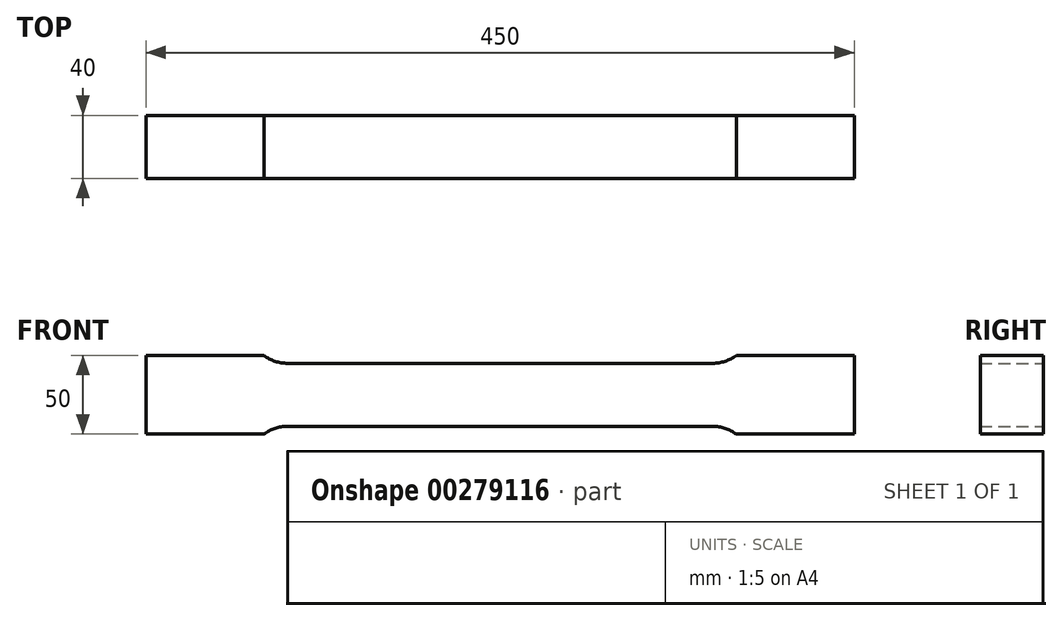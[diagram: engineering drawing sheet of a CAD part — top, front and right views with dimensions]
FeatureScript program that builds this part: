
annotation { "Feature Type Name" : "Feature", "Feature Type Description" : "" }
export const myFeature = defineFeature(function(context is Context, id is Id, definition is map)
    precondition{}
    {
        {
            var Q0;
            Q0=qCreatedBy(makeId("Front.planeOp"),FACE);
            var sketch = newSketch(context, id + "F0", { "sketchPlane" : qUnion([Q0])});
            skLineSegment(sketch, "E0", {"start": v(0, 20) * mm, "end": v(135, 20) * mm});
            skArc(sketch, "E1", {"start": v(135, 20) * mm, "mid": v(142.9, 21.28) * mm, "end": v(150, 25) * mm});
            skLineSegment(sketch, "E2", {"start": v(150, 25) * mm, "end": v(225, 25) * mm});
            skLineSegment(sketch, "E3", {"start": v(225, 25) * mm, "end": v(225, 0) * mm});
            skLineSegment(sketch, "E4.MirrorCS", {"start": v(150, -25) * mm, "end": v(225, -25) * mm});
            skLineSegment(sketch, "E5.MirrorCS", {"start": v(225, -25) * mm, "end": v(225, 0) * mm});
            skLineSegment(sketch, "E6.MirrorCS", {"start": v(0, -20) * mm, "end": v(135, -20) * mm});
            skArc(sketch, "E7.MirrorCS", {"start": v(135, -20) * mm, "mid": v(142.9, -21.28) * mm, "end": v(150, -25) * mm});
            skLineSegment(sketch, "E8.MirrorCS", {"start": v(-150, -25) * mm, "end": v(-225, -25) * mm});
            skLineSegment(sketch, "E9.MirrorCS", {"start": v(-225, -25) * mm, "end": v(-225, 0) * mm});
            skLineSegment(sketch, "E10.MirrorCS", {"start": v(-225, 25) * mm, "end": v(-225, 0) * mm});
            skLineSegment(sketch, "E11.MirrorCS", {"start": v(-150, 25) * mm, "end": v(-225, 25) * mm});
            skArc(sketch, "E12.MirrorCS", {"start": v(-135, 20) * mm, "mid": v(-142.9, 21.28) * mm, "end": v(-150, 25) * mm});
            skLineSegment(sketch, "E13.MirrorCS", {"start": v(0, -20) * mm, "end": v(-135, -20) * mm});
            skLineSegment(sketch, "E14.MirrorCS", {"start": v(0, 20) * mm, "end": v(-135, 20) * mm});
            skArc(sketch, "E15.MirrorCS", {"start": v(-135, -20) * mm, "mid": v(-142.9, -21.28) * mm, "end": v(-150, -25) * mm});
            skSolve(sketch);
        }
        {
            var Q0;
            Q0 = qSketchRegion(id + "F0", true);
            extrude(context, id + "F1", {"entities" : qUnion([Q0]), "endBound" : BoundingType.SYMMETRIC, "depth" : 40 * mm});
        }
    });
